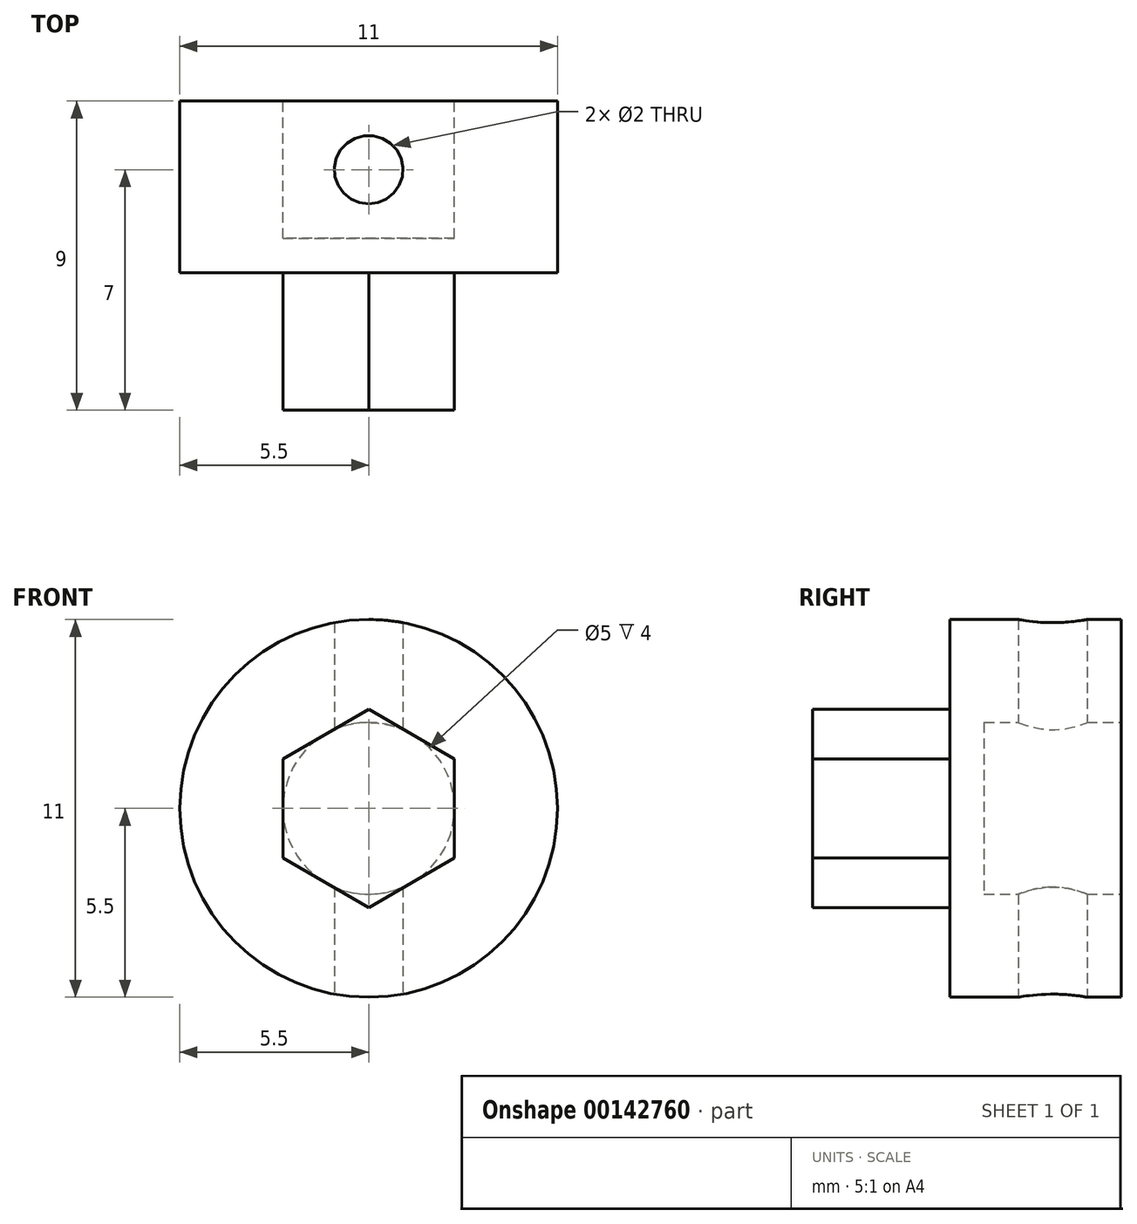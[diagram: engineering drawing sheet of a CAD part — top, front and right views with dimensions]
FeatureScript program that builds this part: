
annotation { "Feature Type Name" : "Feature", "Feature Type Description" : "" }
export const myFeature = defineFeature(function(context is Context, id is Id, definition is map)
    precondition{}
    {
        {
            var Q0;
            Q0=qCreatedBy(makeId("Front.planeOp"),FACE);
            var sketch = newSketch(context, id + "F0", { "sketchPlane" : qUnion([Q0])});
            skCircle(sketch, "E0", {"center": v(0, 0) * mm, "radius": 5.5 * mm});
            skCircle(sketch, "E1", {"center": v(0, 0) * mm, "radius": 2.7 * mm, "construction": true});
            skSolve(sketch);
        }
        {
            var Q0;
            Q0 = qSketchRegion(id + "F0", true);
            var Q1;
            Q1=makeQuery(id+"F0.imprint","IMPRINT",FACE,{"disambiguationData":[TD([[makeQuery(id+"F0.imprint","IMPRINT",EDGE,{"derivedFrom":sQuery(id+"F0.wireOp",EDGE,"E0")}),1.0]])]});
            extrude(context, id + "F1", {"entities" : qUnion([Q0, Q1]), "depth" : 5 * mm});
        }
        {
            var Q0;
            Q0=makeQuery(id+"F1.opExtrude","CAP_FACE",FACE,{"disambiguationData":[OSD([sQuery(id+"F0.wireOp",EDGE,"E0")])],"isStart":false});
            var sketch = newSketch(context, id + "F2", { "sketchPlane" : qUnion([Q0])});
            skCircle(sketch, "E2.cCircle", {"center": v(0, 0) * mm, "radius": 2.5 * mm, "construction": true});
            skLineSegment(sketch, "E2.0", {"start": v(2.5, 1.44) * mm, "end": v(2.5, -1.44) * mm});
            skLineSegment(sketch, "E2.1", {"start": v(2.5, -1.44) * mm, "end": v(0, -2.89) * mm});
            skLineSegment(sketch, "E2.2", {"start": v(0, -2.89) * mm, "end": v(-2.5, -1.44) * mm});
            skLineSegment(sketch, "E2.3", {"start": v(-2.5, -1.44) * mm, "end": v(-2.5, 1.44) * mm});
            skLineSegment(sketch, "E2.4", {"start": v(-2.5, 1.44) * mm, "end": v(0, 2.89) * mm});
            skLineSegment(sketch, "E2.5", {"start": v(0, 2.89) * mm, "end": v(2.5, 1.44) * mm});
            skPoint(sketch, "E2.0.midPoint", {"position": v(2.5, 0) * mm});
            skSolve(sketch);
        }
        {
            var Q0;
            Q0=makeQuery(id+"F2.imprint","IMPRINT",FACE,{"disambiguationData":[TD([[makeQuery(id+"F2.imprint","IMPRINT",EDGE,{"derivedFrom":sQuery(id+"F2.wireOp",EDGE,"E2.0")}),-1.0]])]});
            extrude(context, id + "F3", {"entities" : qUnion([Q0]), "operationType" : NewBodyOperationType.ADD, "depth" : 4 * mm});
        }
        {
            var Q0;
            Q0=makeQuery(id+"F1.opExtrude","CAP_FACE",FACE,{"disambiguationData":[OSD([sQuery(id+"F0.wireOp",EDGE,"E0")])],"isStart":true});
            var sketch = newSketch(context, id + "F4", { "sketchPlane" : qUnion([Q0])});
            skCircle(sketch, "E3", {"center": v(0, 0) * mm, "radius": 2.5 * mm});
            skSolve(sketch);
        }
        {
            var Q0;
            Q0=makeQuery(id+"F4.imprint","IMPRINT",FACE,{"disambiguationData":[TD([[makeQuery(id+"F4.imprint","IMPRINT",EDGE,{"derivedFrom":sQuery(id+"F4.wireOp",EDGE,"E3")}),1.0]])]});
            extrude(context, id + "F5", {"entities" : qUnion([Q0]), "operationType" : NewBodyOperationType.REMOVE, "oppositeDirection" : true, "depth" : 4 * mm});
        }
        {
            var Q0;
            Q0=qCreatedBy(makeId("Top.planeOp"),FACE);
            var sketch = newSketch(context, id + "F6", { "sketchPlane" : qUnion([Q0])});
            skCircle(sketch, "E4", {"center": v(0, -2) * mm, "radius": 1 * mm});
            skSolve(sketch);
        }
        {
            var Q0;
            Q0 = qSketchRegion(id + "F6", true);
            extrude(context, id + "F7", {"entities" : qUnion([Q0]), "operationType" : NewBodyOperationType.REMOVE, "endBound" : BoundingType.THROUGH_ALL, "depth" : 25 * mm, "hasSecondDirection" : true, "secondDirectionBound" : SecondDirectionBoundingType.THROUGH_ALL, "secondDirectionOppositeDirection" : true, "secondDirectionDepth" : 25 * mm});
        }
    });
